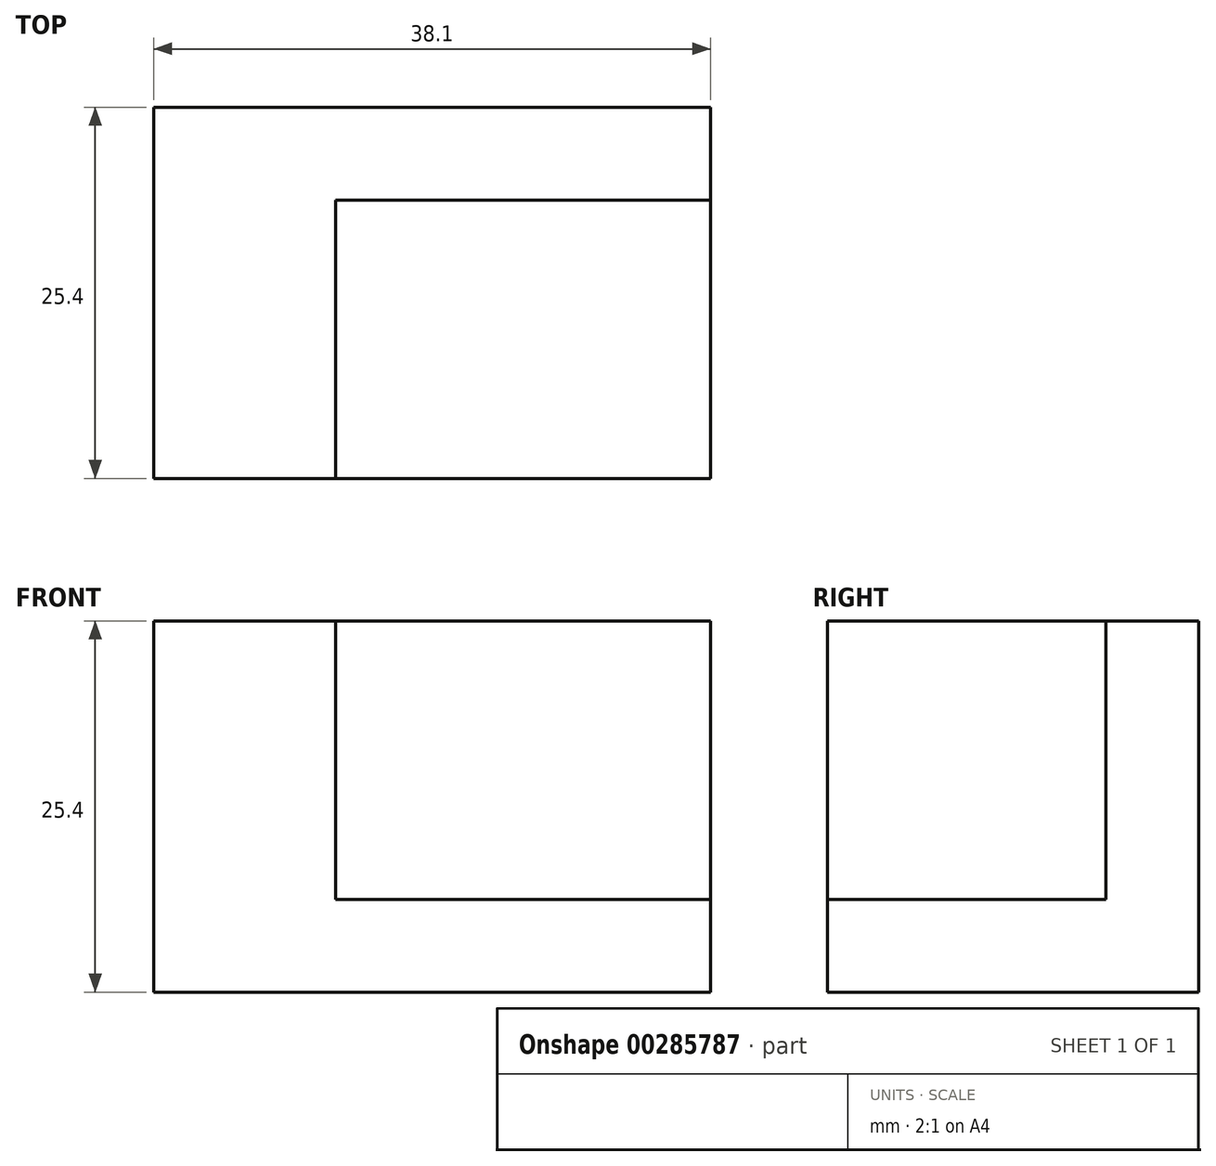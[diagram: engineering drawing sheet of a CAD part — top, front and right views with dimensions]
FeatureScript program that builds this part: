
annotation { "Feature Type Name" : "Feature", "Feature Type Description" : "" }
export const myFeature = defineFeature(function(context is Context, id is Id, definition is map)
    precondition{}
    {
        {
            var Q0;
            Q0=qCreatedBy(makeId("Front.planeOp"),FACE);
            var sketch = newSketch(context, id + "F0", { "sketchPlane" : qUnion([Q0])});
            skLineSegment(sketch, "E0", {"start": v(0, 0) * mm, "end": v(0, 25.4) * mm});
            skLineSegment(sketch, "E1", {"start": v(0, 25.4) * mm, "end": v(38.1, 25.4) * mm});
            skLineSegment(sketch, "E2", {"start": v(38.1, 25.4) * mm, "end": v(38.1, 0) * mm});
            skLineSegment(sketch, "E3", {"start": v(0, 0) * mm, "end": v(38.1, 0) * mm});
            skSolve(sketch);
        }
        {
            var Q0;
            Q0 = qSketchRegion(id + "F0", true);
            extrude(context, id + "F1", {"entities" : qUnion([Q0]), "oppositeDirection" : true, "depth" : 25.4 * mm});
        }
        {
            var Q0;
            Q0=qCreatedBy(makeId("Top.planeOp"),FACE);
            var sketch = newSketch(context, id + "F2", { "sketchPlane" : qUnion([Q0])});
            skLineSegment(sketch, "E4", {"start": v(38.1, 0) * mm, "end": v(38.1, 19.05) * mm});
            skLineSegment(sketch, "E5", {"start": v(38.1, 19.05) * mm, "end": v(12.46, 19.05) * mm});
            skLineSegment(sketch, "E6", {"start": v(12.46, 19.05) * mm, "end": v(12.46, 0) * mm});
            skLineSegment(sketch, "E7", {"start": v(12.46, 0) * mm, "end": v(38.1, 0) * mm});
            skSolve(sketch);
        }
        {
            var Q0;
            Q0 = qSketchRegion(id + "F2", true);
            extrude(context, id + "F3", {"entities" : qUnion([Q0]), "operationType" : NewBodyOperationType.REMOVE, "depth" : 25.4 * mm, "hasSecondDirection" : true, "secondDirectionOppositeDirection" : false, "secondDirectionDepth" : 6.35 * mm});
        }
    });
